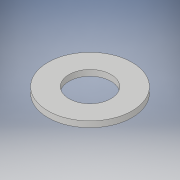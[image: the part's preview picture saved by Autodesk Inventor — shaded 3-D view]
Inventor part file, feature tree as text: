
AUTODESK INVENTOR PART (.ipt)
format: ipt  version: 2017 (Build 210142000, 142)  size: 96,768 bytes
history: native  units: in
note: dims shown in document units (in); Inventor stores cm internally (conversion verified against a paired STEP export)
features: extrude x1, sketch x1
ambient origin geometry x8: Origin, YZ Plane, XZ Plane, XY Plane, X Axis, Y Axis, Z Axis, Center Point
bodies: Solid1 (feature_tree)
feature tree (2):
  extrude  "Extrusion1"  Depth=0.035in
  sketch  "Sketch1"  dims[d0=0.25in d1=0.5in d2=0.035in d3=0.0in]
